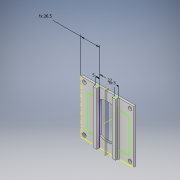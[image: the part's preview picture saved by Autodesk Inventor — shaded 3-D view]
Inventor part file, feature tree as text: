
AUTODESK INVENTOR PART (.ipt)
format: ipt  version: 2019 (Build 230136000, 136)  size: 168,448 bytes
history: native  units: mm
features: extrude x3, other x2, sketch x2, plane x1, mirror x1, fillet x1
ambient origin geometry x8: Origin, YZ Plane, XZ Plane, XY Plane, X Axis, Y Axis, Z Axis, Center Point
bodies: Body1 (feature_tree), Body2 (feature_tree), Body3 (feature_tree)
feature tree (10):
  other  "50x5 interface.ipt"
  extrude  "Extrusion1"  Depth=3.0mm TaperAngle=0.0deg
  sketch  "Sketch3"  dims[d4=5.0mm d5=3.0mm d6=0.0mm d7=4.0mm d8=0.0mm d9=90.0deg d11=26.5mm d13=5.0mm d14=22.0mm d15=4.0mm d16=0.0mm d17=2.0mm]
  extrude  "Extrusion2"  Depth=3.0mm TaperAngle=0.0deg
  plane  "Work Plane2"
  mirror  "Mirror1"
  extrude  "Extrusion3"  Depth=4.0mm TaperAngle=0.0deg
  fillet  "Fillet1"  [1 undecoded]
  sketch  "Sketch1"  dims[d1=10.0mm d2=3.0mm d3=0.0mm]
  other  "Work Axis1"
note: 1 required parameter value undecoded (feature->parameter linkage not recoverable at this tier; creation-order binding heuristic only, values carry confidence <= 0.55)
